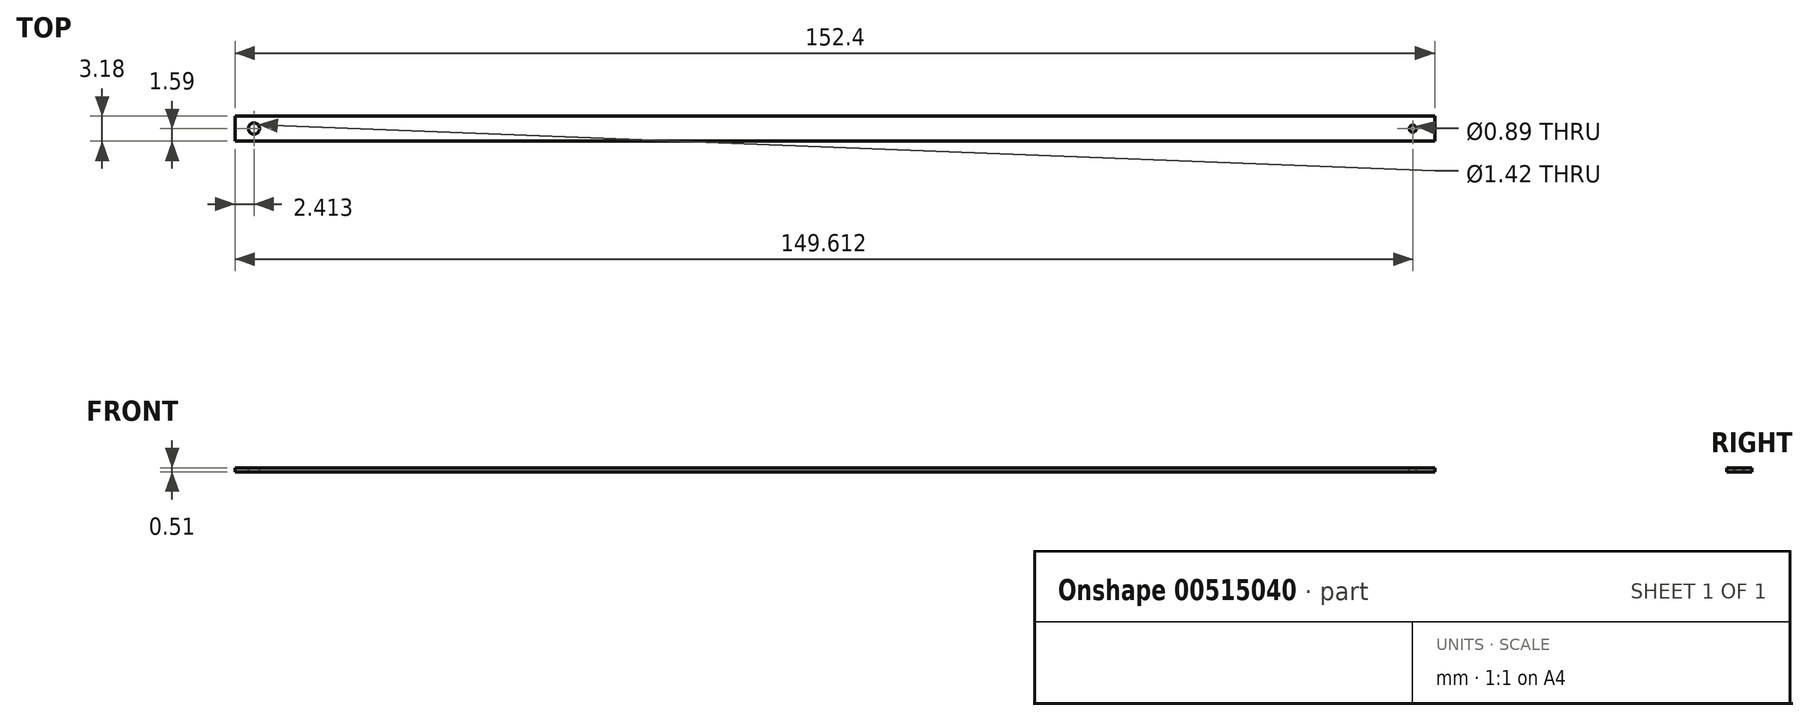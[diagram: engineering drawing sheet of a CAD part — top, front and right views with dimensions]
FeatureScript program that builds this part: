
annotation { "Feature Type Name" : "Feature", "Feature Type Description" : "" }
export const myFeature = defineFeature(function(context is Context, id is Id, definition is map)
    precondition{}
    {
        {
            var Q0;
            Q0=qCreatedBy(makeId("Top.planeOp"),FACE);
            var sketch = newSketch(context, id + "F0", { "sketchPlane" : qUnion([Q0])});
            skLineSegment(sketch, "E0.bottom", {"start": v(76.2, 1.59) * mm, "end": v(-76.2, 1.59) * mm});
            skLineSegment(sketch, "E0.top", {"start": v(76.2, -1.59) * mm, "end": v(-76.2, -1.59) * mm});
            skLineSegment(sketch, "E0.left", {"start": v(76.2, 1.59) * mm, "end": v(76.2, -1.59) * mm});
            skLineSegment(sketch, "E0.right", {"start": v(-76.2, 1.59) * mm, "end": v(-76.2, -1.59) * mm});
            skPoint(sketch, "E0.middle", {"position": v(0, 0) * mm});
            skSolve(sketch);
        }
        {
            var Q0;
            Q0=makeQuery(id+"F0.imprint","IMPRINT",FACE,{"disambiguationData":[TD([[makeQuery(id+"F0.imprint","IMPRINT",EDGE,{"derivedFrom":sQuery(id+"F0.wireOp",EDGE,"E0.bottom")}),1.0]])]});
            extrude(context, id + "F1", {"entities" : qUnion([Q0]), "depth" : 0.5 * mm, "offsetDistance" : 25.4 * mm});
        }
        {
            var Q0;
            Q0=makeQuery(id+"F1.opExtrude","CAP_FACE",FACE,{"disambiguationData":[OSD([sQuery(id+"F0.wireOp",EDGE,"E0.bottom"),sQuery(id+"F0.wireOp",EDGE,"E0.top"),sQuery(id+"F0.wireOp",EDGE,"E0.left"),sQuery(id+"F0.wireOp",EDGE,"E0.right")])],"isStart":false});
            var sketch = newSketch(context, id + "F2", { "sketchPlane" : qUnion([Q0])});
            skCircle(sketch, "E1", {"center": v(73.41, 0) * mm, "radius": 0.45 * mm});
            skSolve(sketch);
        }
        {
            var Q0;
            Q0 = qSketchRegion(id + "F2", true);
            extrude(context, id + "F3", {"entities" : qUnion([Q0]), "operationType" : NewBodyOperationType.REMOVE, "oppositeDirection" : true, "depth" : 25.4 * mm, "offsetDistance" : 25.4 * mm});
        }
        {
            var Q0;
            Q0=makeQuery(id+"F1.opExtrude","CAP_FACE",FACE,{"disambiguationData":[OSD([sQuery(id+"F0.wireOp",EDGE,"E0.bottom"),sQuery(id+"F0.wireOp",EDGE,"E0.top"),sQuery(id+"F0.wireOp",EDGE,"E0.left"),sQuery(id+"F0.wireOp",EDGE,"E0.right")])],"isStart":false});
            var sketch = newSketch(context, id + "F4", { "sketchPlane" : qUnion([Q0])});
            skCircle(sketch, "E2", {"center": v(-73.79, 0) * mm, "radius": 0.71 * mm});
            skSolve(sketch);
        }
        {
            var Q0;
            Q0 = qSketchRegion(id + "F4", true);
            extrude(context, id + "F5", {"entities" : qUnion([Q0]), "operationType" : NewBodyOperationType.REMOVE, "oppositeDirection" : true, "depth" : 25.4 * mm, "offsetDistance" : 25.4 * mm});
        }
    });
